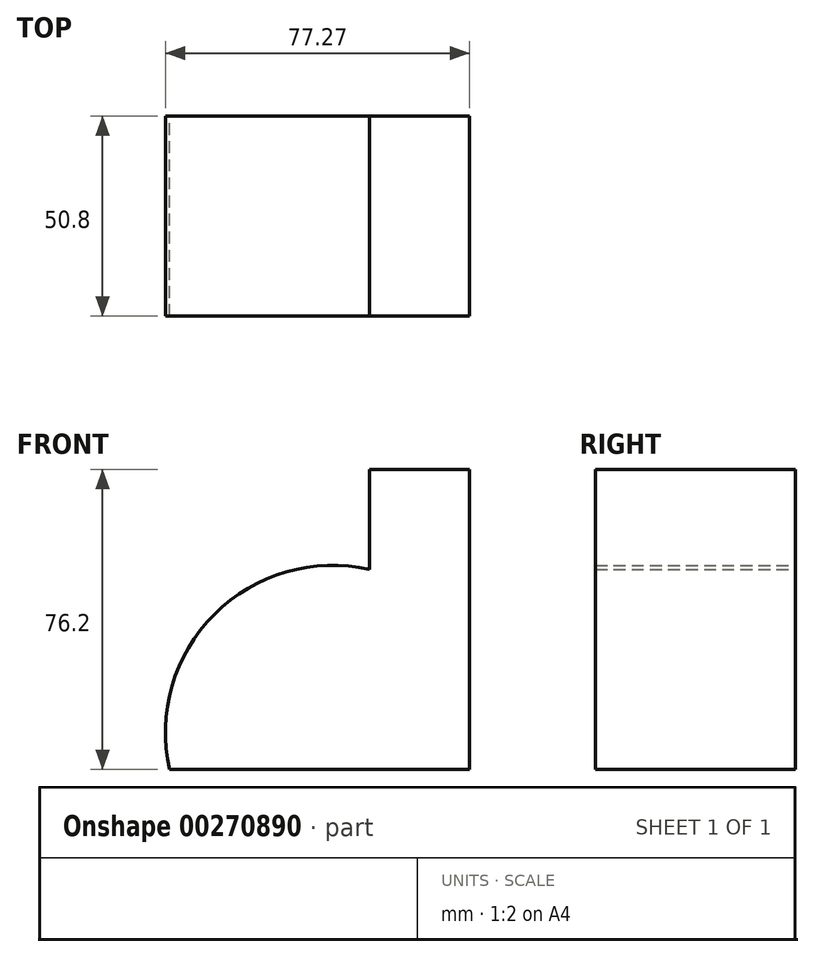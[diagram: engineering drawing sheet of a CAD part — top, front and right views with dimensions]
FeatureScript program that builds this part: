
annotation { "Feature Type Name" : "Feature", "Feature Type Description" : "" }
export const myFeature = defineFeature(function(context is Context, id is Id, definition is map)
    precondition{}
    {
        {
            var Q0;
            Q0=qCreatedBy(makeId("Front.planeOp"),FACE);
            var sketch = newSketch(context, id + "F0", { "sketchPlane" : qUnion([Q0])});
            skLineSegment(sketch, "E0", {"start": v(0, 0) * mm, "end": v(-76.2, 0) * mm});
            skLineSegment(sketch, "E1", {"start": v(0, 0) * mm, "end": v(0, 76.2) * mm});
            skLineSegment(sketch, "E2", {"start": v(0, 76.2) * mm, "end": v(-25.4, 76.2) * mm});
            skLineSegment(sketch, "E3", {"start": v(-25.4, 76.2) * mm, "end": v(-25.4, 50.8) * mm});
            skArc(sketch, "E4", {"start": v(-25.4, 50.8) * mm, "mid": v(-64.84, 39.44) * mm, "end": v(-76.2, 0) * mm});
            skSolve(sketch);
        }
        {
            var Q0;
            Q0 = qSketchRegion(id + "F0", true);
            extrude(context, id + "F1", {"entities" : qUnion([Q0]), "depth" : 50.8 * mm});
        }
    });
